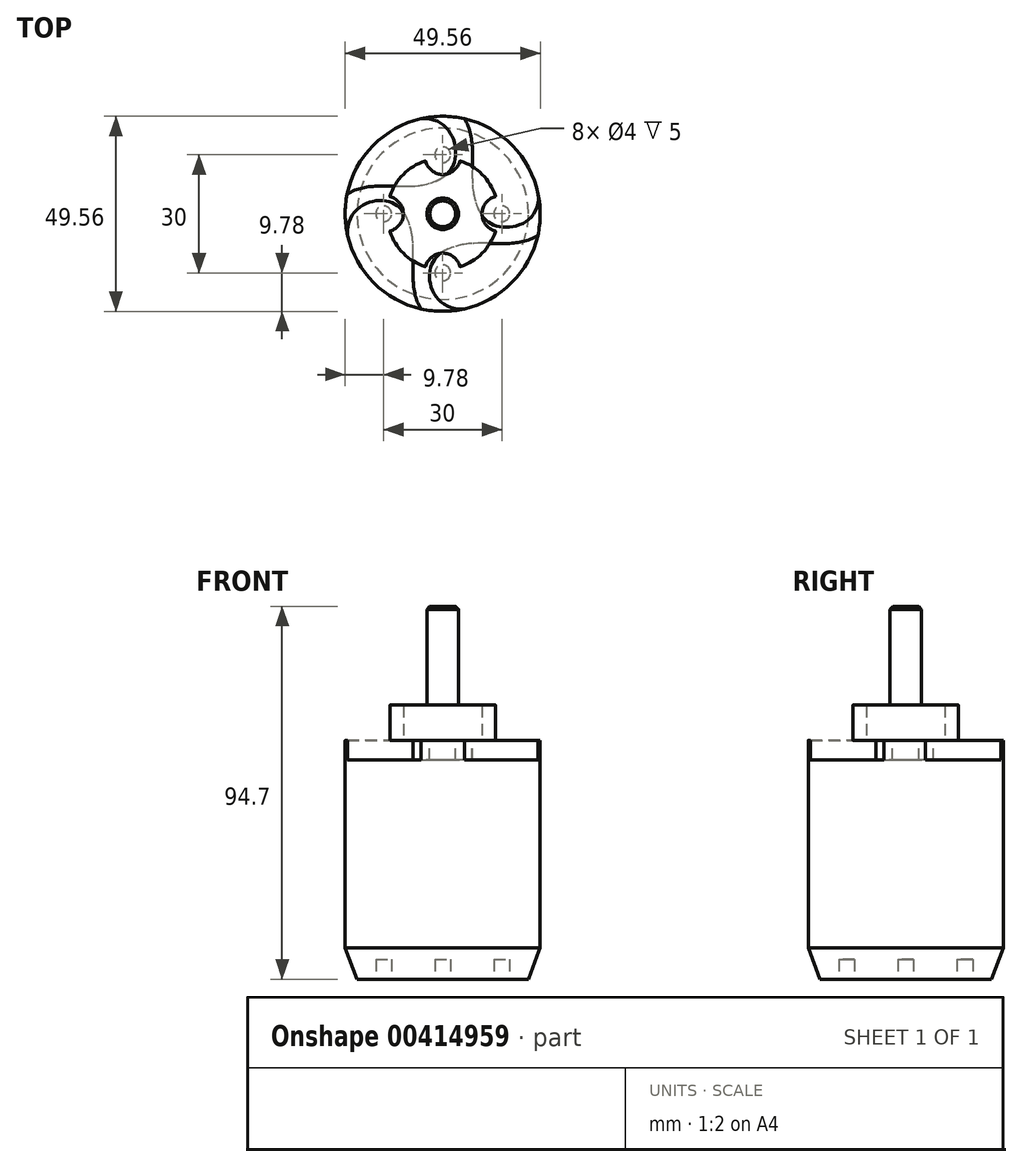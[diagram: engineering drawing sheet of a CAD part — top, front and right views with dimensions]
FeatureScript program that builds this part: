
annotation { "Feature Type Name" : "Feature", "Feature Type Description" : "" }
export const myFeature = defineFeature(function(context is Context, id is Id, definition is map)
    precondition{}
    {
        {
            var Q0;
            Q0=qCreatedBy(makeId("Top.planeOp"),FACE);
            var sketch = newSketch(context, id + "F0", { "sketchPlane" : qUnion([Q0])});
            skCircle(sketch, "E0", {"center": v(0, 0) * mm, "radius": 24.77 * mm});
            skSolve(sketch);
        }
        {
            var Q0;
            Q0 = qSketchRegion(id + "F0", true);
            extrude(context, id + "F1", {"entities" : qUnion([Q0]), "depth" : 60.7 * mm});
        }
        {
            var Q0;
            Q0=makeQuery(id+"F1.opExtrude","CAP_EDGE",EDGE,{"disambiguationData":[OSD([sQuery(id+"F0.wireOp",EDGE,"E0")])],"isStart":true});
            chamfer(context, id + "F2", {"entities" : qUnion([Q0]), "chamferType" : ChamferType.TWO_OFFSETS, "width1" : 3 * mm, "oppositeDirection" : true, "width2" : 8 * mm, "tangentPropagation" : true});
        }
        {
            var Q0;
            Q0=makeQuery(id+"F1.opExtrude","CAP_FACE",FACE,{"disambiguationData":[OSD([sQuery(id+"F0.wireOp",EDGE,"E0")])],"isStart":false});
            var sketch = newSketch(context, id + "F3", { "sketchPlane" : qUnion([Q0])});
            skCircle(sketch, "E1", {"center": v(0, 0) * mm, "radius": 10 * mm, "construction": true});
            skLineSegment(sketch, "E2", {"start": v(-29.63, 0) * mm, "end": v(38.04, 0) * mm, "construction": true});
            skLineSegment(sketch, "E3", {"start": v(0, 27.73) * mm, "end": v(0, -25.72) * mm, "construction": true});
            skLineSegment(sketch, "E4.0", {"start": v(-5.5, 27.73) * mm, "end": v(-5.5, -25.72) * mm, "construction": true});
            skLineSegment(sketch, "E5.0", {"start": v(5.5, 27.73) * mm, "end": v(5.5, -25.72) * mm, "construction": true});
            skLineSegment(sketch, "E6.0", {"start": v(-29.63, -5.5) * mm, "end": v(38.04, -5.5) * mm, "construction": true});
            skLineSegment(sketch, "E7.0", {"start": v(-29.63, 5) * mm, "end": v(38.04, 5) * mm, "construction": true});
            skCircle(sketch, "E8.0.0", {"center": v(0, 0) * mm, "radius": 24.77 * mm, "construction": true});
            skLineSegment(sketch, "E9", {"start": v(24.27, 5) * mm, "end": v(-24.16, -5.5) * mm, "construction": true});
            skLineSegment(sketch, "E10", {"start": v(-5.5, 24.16) * mm, "end": v(5.5, -24.16) * mm, "construction": true});
            skLineSegment(sketch, "E11", {"start": v(5.5, 24.16) * mm, "end": v(-5.5, -24.16) * mm, "construction": true});
            skLineSegment(sketch, "E12", {"start": v(-24.27, 5) * mm, "end": v(24.16, -5.5) * mm, "construction": true});
            skFitSpline(sketch, "E13", {"points": [v(-24.27, 5) * mm, v(-7.05, 7.1) * mm, v(3.04, 13.37) * mm, v(-5.5, 24.16) * mm], "startDerivative": vector(40.33, 25.93) * mm, "endDerivative": vector(-64.92, -5.2) * mm});
            skFitSpline(sketch, "E14", {"points": [v(5.5, 24.16) * mm, v(7.6, 6.94) * mm, v(13.87, -3.15) * mm, v(24.27, 5) * mm], "startDerivative": vector(25.93, -40.33) * mm, "endDerivative": vector(-5.2, 64.92) * mm});
            skFitSpline(sketch, "E15", {"points": [v(24.16, -5.5) * mm, v(6.94, -7.6) * mm, v(-3.15, -13.87) * mm, v(5.5, -24.16) * mm], "startDerivative": vector(-40.33, -25.93) * mm, "endDerivative": vector(64.92, 5.2) * mm});
            skFitSpline(sketch, "E16", {"points": [v(-5.5, -24.16) * mm, v(-7.6, -6.94) * mm, v(-13.87, 3.15) * mm, v(-24.16, -5.5) * mm], "startDerivative": vector(-25.93, 40.33) * mm, "endDerivative": vector(5.2, -64.92) * mm});
            skArc(sketch, "E17", {"start": v(-5.5, 24.16) * mm, "mid": v(-17.7, 17.34) * mm, "end": v(-24.27, 5) * mm});
            skArc(sketch, "E18", {"start": v(-24.16, -5.5) * mm, "mid": v(-17.52, -17.52) * mm, "end": v(-5.5, -24.16) * mm});
            skArc(sketch, "E19", {"start": v(5.5, -24.16) * mm, "mid": v(17.52, -17.52) * mm, "end": v(24.16, -5.5) * mm});
            skArc(sketch, "E20", {"start": v(24.27, 5) * mm, "mid": v(17.7, 17.34) * mm, "end": v(5.5, 24.16) * mm});
            skSolve(sketch);
        }
        {
            var Q0;
            Q0=makeQuery(id+"F1.opExtrude","CAP_FACE",FACE,{"disambiguationData":[OSD([sQuery(id+"F0.wireOp",EDGE,"E0")])],"isStart":false});
            var sketch = newSketch(context, id + "F4", { "sketchPlane" : qUnion([Q0])});
            skArc(sketch, "E21", {"start": v(-13.42, -4.48) * mm, "mid": v(-10, -10) * mm, "end": v(-4.48, -13.42) * mm});
            skCircle(sketch, "E22", {"center": v(0, 0) * mm, "radius": 10 * mm, "construction": true});
            skLineSegment(sketch, "E23", {"start": v(-33.16, 0) * mm, "end": v(34.34, 0) * mm, "construction": true});
            skLineSegment(sketch, "E24", {"start": v(0, 37) * mm, "end": v(0, -35.53) * mm, "construction": true});
            skArc(sketch, "E25", {"start": v(-13.35, -4.35) * mm, "mid": v(-10, 0) * mm, "end": v(-13.35, 4.35) * mm});
            skArc(sketch, "E26", {"start": v(-4.35, 13.35) * mm, "mid": v(0, 10) * mm, "end": v(4.35, 13.35) * mm});
            skArc(sketch, "E27", {"start": v(13.35, 4.35) * mm, "mid": v(10, 0) * mm, "end": v(13.35, -4.35) * mm});
            skArc(sketch, "E28", {"start": v(4.35, -13.35) * mm, "mid": v(0, -10) * mm, "end": v(-4.35, -13.35) * mm});
            skArc(sketch, "E29.trimOffspring", {"start": v(-4.48, 13.42) * mm, "mid": v(-10, 10) * mm, "end": v(-13.42, 4.48) * mm});
            skArc(sketch, "E30.trimOffspring", {"start": v(13.42, 4.48) * mm, "mid": v(10, 10) * mm, "end": v(4.48, 13.42) * mm});
            skArc(sketch, "E31.trimOffspring", {"start": v(4.48, -13.42) * mm, "mid": v(10, -10) * mm, "end": v(13.42, -4.48) * mm});
            skPoint(sketch, "E32.visualSharp", {"position": v(-13.46, 4.38) * mm});
            skArc(sketch, "E32.filletArc", {"start": v(-13.42, 4.48) * mm, "mid": v(-13.42, 4.4) * mm, "end": v(-13.35, 4.35) * mm});
            skPoint(sketch, "E33.visualSharp", {"position": v(-4.38, 13.46) * mm});
            skArc(sketch, "E33.filletArc", {"start": v(-4.35, 13.35) * mm, "mid": v(-4.4, 13.42) * mm, "end": v(-4.48, 13.42) * mm});
            skPoint(sketch, "E34.visualSharp", {"position": v(4.38, 13.46) * mm});
            skArc(sketch, "E34.filletArc", {"start": v(4.48, 13.42) * mm, "mid": v(4.4, 13.42) * mm, "end": v(4.35, 13.35) * mm});
            skPoint(sketch, "E35.visualSharp", {"position": v(13.46, 4.38) * mm});
            skArc(sketch, "E35.filletArc", {"start": v(13.35, 4.35) * mm, "mid": v(13.42, 4.4) * mm, "end": v(13.42, 4.48) * mm});
            skPoint(sketch, "E36.visualSharp", {"position": v(13.46, -4.38) * mm});
            skArc(sketch, "E36.filletArc", {"start": v(13.42, -4.48) * mm, "mid": v(13.42, -4.4) * mm, "end": v(13.35, -4.35) * mm});
            skPoint(sketch, "E37.visualSharp", {"position": v(4.38, -13.46) * mm});
            skArc(sketch, "E37.filletArc", {"start": v(4.35, -13.35) * mm, "mid": v(4.4, -13.42) * mm, "end": v(4.48, -13.42) * mm});
            skPoint(sketch, "E38.visualSharp", {"position": v(-4.38, -13.46) * mm});
            skArc(sketch, "E38.filletArc", {"start": v(-4.48, -13.42) * mm, "mid": v(-4.4, -13.42) * mm, "end": v(-4.35, -13.35) * mm});
            skPoint(sketch, "E39.visualSharp", {"position": v(-13.46, -4.38) * mm});
            skArc(sketch, "E39.filletArc", {"start": v(-13.35, -4.35) * mm, "mid": v(-13.42, -4.4) * mm, "end": v(-13.42, -4.48) * mm});
            skLineSegment(sketch, "E40", {"start": v(-4.38, -13.46) * mm, "end": v(4.38, -13.46) * mm, "construction": true});
            skLineSegment(sketch, "E41", {"start": v(13.46, 4.38) * mm, "end": v(13.46, -4.38) * mm, "construction": true});
            skSolve(sketch);
        }
        {
            var Q0;
            Q0 = qSketchRegion(id + "F4", true);
            extrude(context, id + "F5", {"entities" : qUnion([Q0]), "depth" : 9 * mm});
        }
        {
            var Q0;
            Q0=makeQuery(id+"F5.opExtrude","CAP_FACE",FACE,{"disambiguationData":[OSD([sQuery(id+"F4.wireOp",EDGE,"E21")])],"isStart":false});
            var sketch = newSketch(context, id + "F6", { "sketchPlane" : qUnion([Q0])});
            skCircle(sketch, "E42", {"center": v(0, 0) * mm, "radius": 4 * mm});
            skSolve(sketch);
        }
        {
            var Q0;
            Q0 = qSketchRegion(id + "F6", true);
            extrude(context, id + "F7", {"entities" : qUnion([Q0]), "operationType" : NewBodyOperationType.ADD, "depth" : 25 * mm});
        }
        {
            var Q0;
            Q0=makeQuery(id+"F5.opExtrude","CAP_FACE",FACE,{"disambiguationData":[OSD([sQuery(id+"F4.wireOp",EDGE,"E21"),sQuery(id+"F4.wireOp",EDGE,"E25"),sQuery(id+"F4.wireOp",EDGE,"E26"),sQuery(id+"F4.wireOp",EDGE,"E27"),sQuery(id+"F4.wireOp",EDGE,"E28"),sQuery(id+"F4.wireOp",EDGE,"E29.trimOffspring"),sQuery(id+"F4.wireOp",EDGE,"E30.trimOffspring"),sQuery(id+"F4.wireOp",EDGE,"E31.trimOffspring"),sQuery(id+"F4.wireOp",EDGE,"E32.filletArc"),sQuery(id+"F4.wireOp",EDGE,"E33.filletArc"),sQuery(id+"F4.wireOp",EDGE,"E34.filletArc"),sQuery(id+"F4.wireOp",EDGE,"E35.filletArc"),sQuery(id+"F4.wireOp",EDGE,"E36.filletArc"),sQuery(id+"F4.wireOp",EDGE,"E37.filletArc"),sQuery(id+"F4.wireOp",EDGE,"E38.filletArc"),sQuery(id+"F4.wireOp",EDGE,"E39.filletArc")])],"isStart":false});
            fillet(context, id + "F8", {"entities" : qUnion([Q0]), "radius" : 0.2 * mm, "tangentPropagation" : true, "allowEdgeOverflow" : false});
        }
        {
            var Q0;
            Q0=makeQuery(id+"F7.opExtrude","CAP_FACE",FACE,{"disambiguationData":[OSD([sQuery(id+"F6.wireOp",EDGE,"E42")])],"isStart":false});
            chamfer(context, id + "F9", {"entities" : qUnion([Q0]), "width" : 0.7 * mm, "tangentPropagation" : true});
        }
        {
            var Q0;
            Q0 = qSketchRegion(id + "F3", true);
            extrude(context, id + "F10", {"entities" : qUnion([Q0]), "operationType" : NewBodyOperationType.REMOVE, "oppositeDirection" : true, "depth" : 5 * mm});
        }
        {
            var Q0;
            Q0=makeQuery(id+"F1.opExtrude","CAP_FACE",FACE,{"disambiguationData":[OSD([sQuery(id+"F0.wireOp",EDGE,"E0")])],"isStart":true});
            var sketch = newSketch(context, id + "F11", { "sketchPlane" : qUnion([Q0])});
            skCircle(sketch, "E43", {"center": v(0, 0) * mm, "radius": 15 * mm, "construction": true});
            skLineSegment(sketch, "E44", {"start": v(-29.24, 0) * mm, "end": v(31.59, 0) * mm, "construction": true});
            skLineSegment(sketch, "E45", {"start": v(0, 34.05) * mm, "end": v(0, -34.34) * mm, "construction": true});
            skCircle(sketch, "E46", {"center": v(0, 15) * mm, "radius": 2 * mm});
            skCircle(sketch, "E47", {"center": v(-15, 0) * mm, "radius": 2 * mm});
            skCircle(sketch, "E48", {"center": v(15, 0) * mm, "radius": 2 * mm});
            skCircle(sketch, "E49", {"center": v(0, -15) * mm, "radius": 2 * mm});
            skSolve(sketch);
        }
        {
            var Q0;
            Q0 = qSketchRegion(id + "F11", true);
            extrude(context, id + "F12", {"entities" : qUnion([Q0]), "operationType" : NewBodyOperationType.REMOVE, "oppositeDirection" : true, "depth" : 5 * mm});
        }
    });
